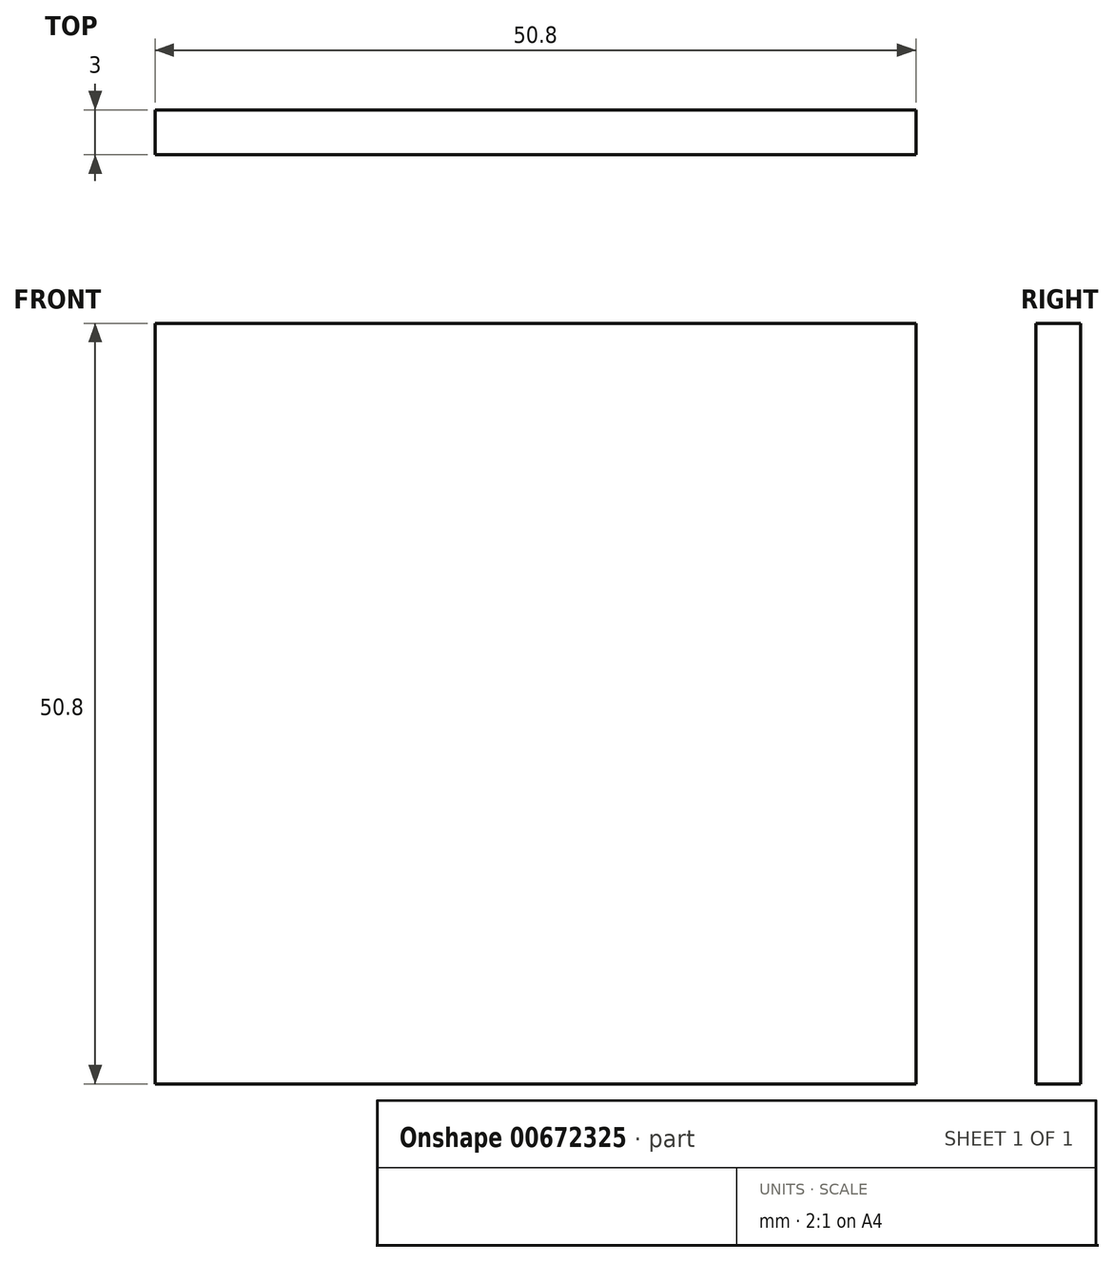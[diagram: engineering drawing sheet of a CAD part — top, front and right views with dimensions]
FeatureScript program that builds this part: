
annotation { "Feature Type Name" : "Feature", "Feature Type Description" : "" }
export const myFeature = defineFeature(function(context is Context, id is Id, definition is map)
    precondition{}
    {
        {
            var Q0;
            Q0=qCreatedBy(makeId("Front.planeOp"),FACE);
            var sketch = newSketch(context, id + "F0", { "sketchPlane" : qUnion([Q0])});
            skLineSegment(sketch, "E0.bottom", {"start": v(-51.02, 7.17) * mm, "end": v(-0.22, 7.17) * mm});
            skLineSegment(sketch, "E0.top", {"start": v(-51.02, -43.63) * mm, "end": v(-0.22, -43.63) * mm});
            skLineSegment(sketch, "E0.left", {"start": v(-51.02, 7.17) * mm, "end": v(-51.02, -43.63) * mm});
            skLineSegment(sketch, "E0.right", {"start": v(-0.22, 7.17) * mm, "end": v(-0.22, -43.63) * mm});
            skSolve(sketch);
        }
        {
            var Q0;
            Q0=makeQuery(id+"F0.imprint","IMPRINT",FACE,{"disambiguationData":[TD([[makeQuery(id+"F0.imprint","IMPRINT",EDGE,{"derivedFrom":sQuery(id+"F0.wireOp",EDGE,"E0.bottom")}),-1.0]])]});
            extrude(context, id + "F1", {"entities" : qUnion([Q0]), "depth" : 3 * mm});
        }
    });
